# Revit family: BC_Hitachi_RAS4-10-HVNP1E_LOD400_
name_source: partatom
category: Equipement de génie climatique
revit_build: Autodesk Revit 2016 (Build: 20150220_1215(x64)
units: mm (PartAtom-declared; Revit-internal decimal feet)

## family parameters
Basée sur le plan de construction = Non
Cote de connecteur circulaire = Utiliser le diamètre
Couper avec des vides une fois chargée = Non
Numéro OmniClass = 23.75.00.00
Partagée = Non
Point de calcul de pièce = Non
Titre OmniClass = Climate Control (HVAC)
Toujours verticalement = Oui
Type d'élément = Normal

## types (5) — shared parameters
Description = The CENTRIFUGE IVX solution has been created for integrate this outdoor group inside the building
Fabricant = HITACHI
Fan diameter = 600.00 mm
Frequency = 50 Hz
Maximum Connected Capacity (%) = 120
Maximum Input Power = 0 W
Minimum Connected Capacity (%) = 50
Modèle = Outdoor Unit - IVX Premium
Overall Depth = 370.00 mm
Overall Height = 1380.00 mm
Overall Width = 950.00 mm
Refrigerant = R410A

## per-type parameters (varying)
- RAS-4HVNP1E: Coefficient Of Performance (COP)=5.16; Commentaires du type=RAS HVNP1E; Cooling Capacity=10 kW; Energy Efficiency Ratio (EER)=4.68; Gas Diameter=15.88 mm; Heating Capacity=11 kW; Height Gas pipe=459.00 mm; Height Liquid pipe=549.00 mm; Liquid Diameter=9.52 mm; Mass=103.00 kg; Maximum AC Voltage=253 V; Maximum Air Flow=80000.0 L/min; Minimum AC Voltage=207 V; Nominal Current=28 A; Nominal Voltage=230 V; Nominal cooling capacity (max)=11 kW; Nominal cooling capacity (min)=5 kW; Nominal cooling power input=1990 W; Nominal heating capacity (max)=14 kW; Nominal heating capacity (min)=5 kW; Nominal heating power input=2020 W; Number of Poles=1; Product Code=7E304020; Recommended circuit breaker=32 A; Refrigerant charge=4.10 kg; Running current cooling=9 A; Running current heating=9 A; Sound power at rated load (dB(A))=65; Sound power dB(A)=65; Sound pressure level Night mode cooling (dB(A))=43; Sound pressure level cooling (dB(A))=47; Sound pressure level heating (dB(A))=49
- RAS-10HNPE: Coefficient Of Performance (COP)=3.84; Commentaires du type=RAS HNPE; Cooling Capacity=25 kW; Energy Efficiency Ratio (EER)=3.07; Gas Diameter=25.40 mm; Heating Capacity=28 kW; Height Gas pipe=465.00 mm; Height Liquid pipe=564.00 mm; Liquid Diameter=12.70 mm; Mass=138.00 kg; Maximum AC Voltage=440 V; Maximum Air Flow=134000.0 L/min; Minimum AC Voltage=360 V; Nominal Current=24 A; Nominal Voltage=400 V; Nominal cooling capacity (max)=28 kW; Nominal cooling capacity (min)=10 kW; Nominal cooling power input=7880 W; Nominal heating capacity (max)=35 kW; Nominal heating capacity (min)=8 kW; Nominal heating power input=7030 W; Number of Poles=3; Product Code=7E310111; Recommended circuit breaker=30 A; Refrigerant charge=6.20 kg; Running current cooling=13 A; Running current heating=11 A; Sound power at rated load (dB(A))=76; Sound power dB(A)=76; Sound pressure level Night mode cooling (dB(A))=56; Sound pressure level cooling (dB(A))=58; Sound pressure level heating (dB(A))=60
- RAS-8HNPE: Coefficient Of Performance (COP)=4.21; Commentaires du type=RAS HNPE; Cooling Capacity=20 kW; Energy Efficiency Ratio (EER)=3.56; Gas Diameter=25.40 mm; Heating Capacity=22 kW; Height Gas pipe=465.00 mm; Height Liquid pipe=546.00 mm; Liquid Diameter=9.52 mm; Mass=136.00 kg; Maximum AC Voltage=440 V; Maximum Air Flow=127000.0 L/min; Minimum AC Voltage=360 V; Nominal Current=24 A; Nominal Voltage=400 V; Nominal cooling capacity (max)=22 kW; Nominal cooling capacity (min)=8 kW; Nominal cooling power input=5360 W; Nominal heating capacity (max)=28 kW; Nominal heating capacity (min)=6 kW; Nominal heating power input=5060 W; Number of Poles=3; Product Code=7E310110; Recommended circuit breaker=30 A; Refrigerant charge=5.70 kg; Running current cooling=9 A; Running current heating=8 A; Sound power at rated load (dB(A))=76; Sound power dB(A)=76; Sound pressure level Night mode cooling (dB(A))=55; Sound pressure level cooling (dB(A))=57; Sound pressure level heating (dB(A))=59
- RAS-6HVNP1E: Coefficient Of Performance (COP)=4.23; Commentaires du type=RAS HVNP1E; Cooling Capacity=14 kW; Energy Efficiency Ratio (EER)=3.41; Gas Diameter=15.88 mm; Heating Capacity=16 kW; Height Gas pipe=459.00 mm; Height Liquid pipe=549.00 mm; Liquid Diameter=9.52 mm; Mass=103.00 kg; Maximum AC Voltage=253 V; Maximum Air Flow=100000.0 L/min; Minimum AC Voltage=207 V; Nominal Current=28 A; Nominal Voltage=230 V; Nominal cooling capacity (max)=16 kW; Nominal cooling capacity (min)=6 kW; Nominal cooling power input=3940 W; Nominal heating capacity (max)=20 kW; Nominal heating capacity (min)=5 kW; Nominal heating power input=3610 W; Number of Poles=1; Product Code=7E304022; Recommended circuit breaker=32 A; Refrigerant charge=4.20 kg; Running current cooling=18 A; Running current heating=16 A; Sound power at rated load (dB(A))=67; Sound power dB(A)=67; Sound pressure level Night mode cooling (dB(A))=45; Sound pressure level cooling (dB(A))=48; Sound pressure level heating (dB(A))=50
- RAS-5HVNP1E: Coefficient Of Performance (COP)=4.55; Commentaires du type=RAS HVNP1E; Cooling Capacity=13 kW; Energy Efficiency Ratio (EER)=3.81; Gas Diameter=15.88 mm; Heating Capacity=14 kW; Height Gas pipe=459.00 mm; Height Liquid pipe=549.00 mm; Liquid Diameter=9.52 mm; Mass=103.00 kg; Maximum AC Voltage=253 V; Maximum Air Flow=90000.0 L/min; Minimum AC Voltage=207 V; Nominal Current=28 A; Nominal Voltage=230 V; Nominal cooling capacity (max)=14 kW; Nominal cooling capacity (min)=6 kW; Nominal cooling power input=3110 W; Nominal heating capacity (max)=18 kW; Nominal heating capacity (min)=5 kW; Nominal heating power input=2910 W; Number of Poles=1; Product Code=7E304021; Recommended circuit breaker=32 A; Refrigerant charge=4.20 kg; Running current cooling=14 A; Running current heating=13 A; Sound power at rated load (dB(A))=66; Sound power dB(A)=66; Sound pressure level Night mode cooling (dB(A))=44; Sound pressure level cooling (dB(A))=48; Sound pressure level heating (dB(A))=50

## geometry (parser evidence)
native form markers: Blend x2
no freeform markers — native parametric forms only
